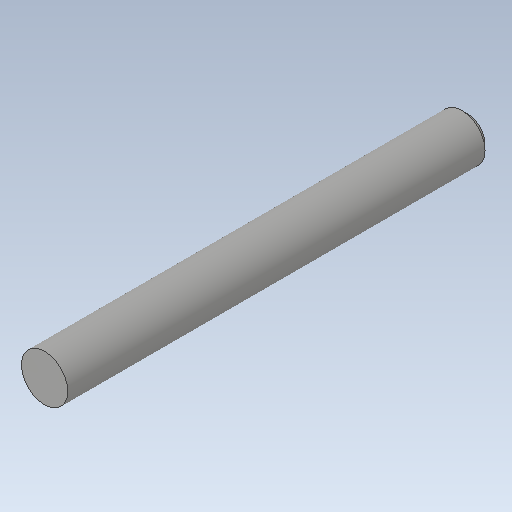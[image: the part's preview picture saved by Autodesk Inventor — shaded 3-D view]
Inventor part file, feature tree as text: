
AUTODESK INVENTOR PART (.ipt)
format: ipt  version: 2020.1 (Build 241239000, 239)  size: 115,712 bytes
history: native  units: mm
features: extrude x1, chamfer x1, sketch x1
ambient origin geometry x8: Origin, YZ Plane, XZ Plane, XY Plane, X Axis, Y Axis, Z Axis, Center Point
bodies: Solid1 (feature_tree)
feature tree (3):
  extrude  "Extrusion1"  Depth=228.0mm
  chamfer  "Chamfer1"  [1 undecoded]
  sketch  "Sketch1"  dims[d0=25.0mm d1=228.0mm d2=0.0mm d3=3.0mm d4=2.0mm d5=45.0deg]
note: 1 required parameter value undecoded (feature->parameter linkage not recoverable at this tier; creation-order binding heuristic only, values carry confidence <= 0.55)
